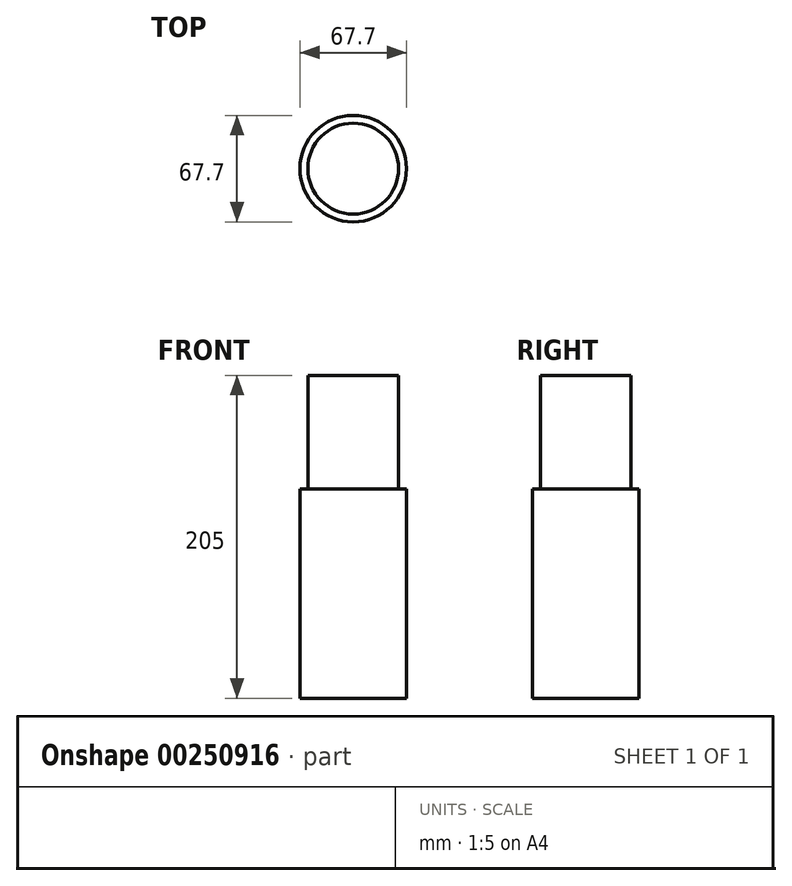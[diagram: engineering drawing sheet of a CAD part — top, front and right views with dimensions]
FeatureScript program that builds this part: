
annotation { "Feature Type Name" : "Feature", "Feature Type Description" : "" }
export const myFeature = defineFeature(function(context is Context, id is Id, definition is map)
    precondition{}
    {
        {
            var Q0;
            Q0=qCreatedBy(makeId("Front.planeOp"),FACE);
            var sketch = newSketch(context, id + "F0", { "sketchPlane" : qUnion([Q0])});
            skLineSegment(sketch, "E0.bottom", {"start": v(33.85, 66.41) * mm, "end": v(-33.85, 66.41) * mm});
            skLineSegment(sketch, "E0.top", {"start": v(33.85, -66.41) * mm, "end": v(-33.85, -66.41) * mm});
            skLineSegment(sketch, "E0.left", {"start": v(33.85, 66.41) * mm, "end": v(33.85, -66.41) * mm});
            skLineSegment(sketch, "E0.right", {"start": v(-33.85, 66.41) * mm, "end": v(-33.85, -66.41) * mm});
            skPoint(sketch, "E0.middle", {"position": v(0, 0) * mm});
            skLineSegment(sketch, "E1", {"start": v(0, 66.41) * mm, "end": v(0, -66.41) * mm});
            skSolve(sketch);
        }
        {
            var Q0;
            {var subQ0=sQuery(id+"F0.wireOp",EDGE,"E0.right");Q0=makeQuery(id+"F0.imprint","IMPRINT",FACE,{"disambiguationData":[TD([[makeQuery(id+"F0.imprint","IMPRINT",EDGE,{"derivedFrom":subQ0}),1.0]])]});}
            var Q1;
            Q1=sQuery(id+"F0.wireOp",EDGE,"E1");
            revolve(context, id + "F1", {"entities" : qUnion([Q0]), "axis" : qUnion([Q1]), "revolveType" : RevolveType.FULL});
        }
        {
            var Q0;
            Q0=makeQuery(id+"F1.opRevolve","SWEPT_FACE",FACE,{"disambiguationData":[OSD([sQuery(id+"F0.wireOp",EDGE,"E0.bottom")])]});
            shell(context, id + "F2", {"entities" : qUnion([Q0]), "thickness" : 5 * mm});
        }
        {
            var Q0;
            Q0=makeQuery(id+"F2.opShell","OFFSET_FACE",FACE,{"disambiguationData":[OSD([sQuery(id+"F0.wireOp",EDGE,"E0.top")])]});
            extrude(context, id + "F3", {"entities" : qUnion([Q0]), "operationType" : NewBodyOperationType.ADD, "depth" : 200 * mm});
        }
    });
